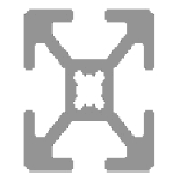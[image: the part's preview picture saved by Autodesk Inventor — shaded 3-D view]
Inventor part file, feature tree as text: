
AUTODESK INVENTOR PART (.ipt)
format: ipt  version: 2013 SP2 (Build 170200200, 200)  size: 234,496 bytes
history: native  units: in
note: dims shown in document units (in); Inventor stores cm internally (conversion verified against a paired STEP export)
features: other x5, sketch x3, plane x1
ambient origin geometry x8: Origin, YZ Plane, XZ Plane, XY Plane, X Axis, Y Axis, Z Axis, Center Point
bodies: Solid1 (feature_tree), Body (feature_tree)
feature tree (9):
  other  "Driven Length"
  other  "Frame Generator"
  other  "Blocks"
  other  "Start Plane"
  other  "End Plane"
  sketch  "Sketch"  dims[d4=0.13in d5=0.0in d6=90.0deg d7=11.0236in]
  sketch  "Sketch2"  dims[d2=0.7874in]
  plane  "Work Plane3"
  sketch  "Sketch3"  dims[d3=11.811in]
